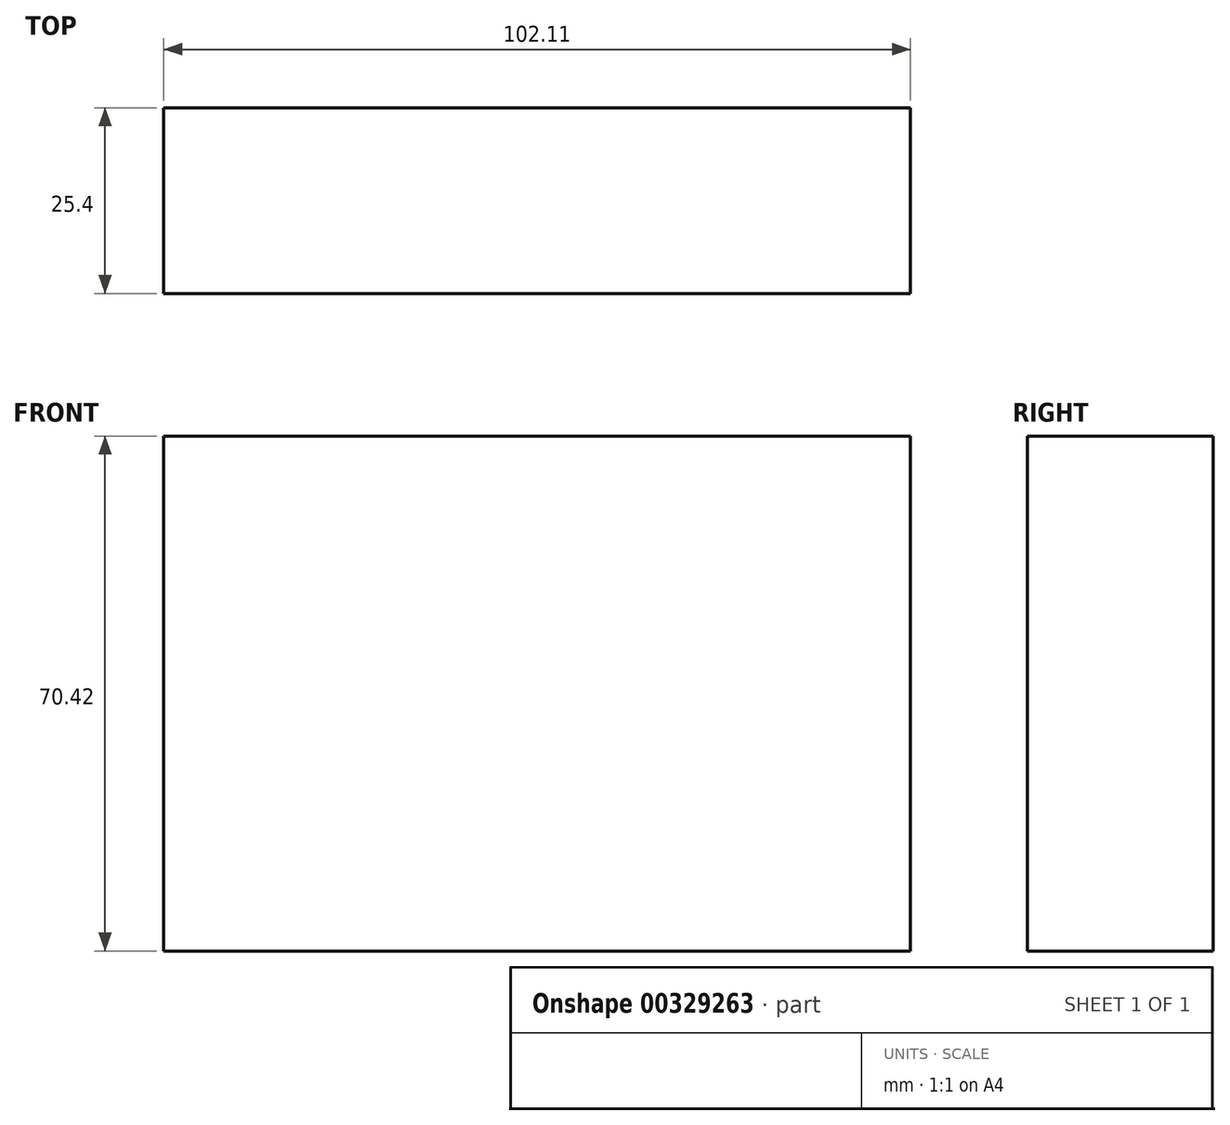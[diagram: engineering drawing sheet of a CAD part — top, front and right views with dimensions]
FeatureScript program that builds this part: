
annotation { "Feature Type Name" : "Feature", "Feature Type Description" : "" }
export const myFeature = defineFeature(function(context is Context, id is Id, definition is map)
    precondition{}
    {
        {
            var Q0;
            Q0=qCreatedBy(makeId("Front.planeOp"),FACE);
            var sketch = newSketch(context, id + "F0", { "sketchPlane" : qUnion([Q0])});
            skLineSegment(sketch, "E0.bottom", {"start": v(-47.99, 36.02) * mm, "end": v(54.12, 36.02) * mm});
            skLineSegment(sketch, "E0.top", {"start": v(-47.99, -34.4) * mm, "end": v(54.12, -34.4) * mm});
            skLineSegment(sketch, "E0.left", {"start": v(-47.99, 36.02) * mm, "end": v(-47.99, -34.4) * mm});
            skLineSegment(sketch, "E0.right", {"start": v(54.12, 36.02) * mm, "end": v(54.12, -34.4) * mm});
            skLineSegment(sketch, "E1.bottom", {"start": v(-25.55, 36.02) * mm, "end": v(0, 36.02) * mm});
            skLineSegment(sketch, "E1.top", {"start": v(-25.55, -16.12) * mm, "end": v(0, -16.12) * mm});
            skLineSegment(sketch, "E1.left", {"start": v(-25.55, 36.02) * mm, "end": v(-25.55, -16.12) * mm});
            skLineSegment(sketch, "E1.right", {"start": v(0, 36.02) * mm, "end": v(0, -16.12) * mm});
            skLineSegment(sketch, "E2.bottom", {"start": v(35.78, 36.02) * mm, "end": v(0, 36.02) * mm});
            skLineSegment(sketch, "E2.top", {"start": v(35.78, 0) * mm, "end": v(0, 0) * mm});
            skLineSegment(sketch, "E2.left", {"start": v(35.78, 36.02) * mm, "end": v(35.78, 0) * mm});
            skLineSegment(sketch, "E2.right", {"start": v(0, 36.02) * mm, "end": v(0, 0) * mm});
            skSolve(sketch);
        }
        {
            var Q0;
            Q0 = qSketchRegion(id + "F0", true);
            extrude(context, id + "F1", {"entities" : qUnion([Q0]), "depth" : 25.4 * mm});
        }
    });
